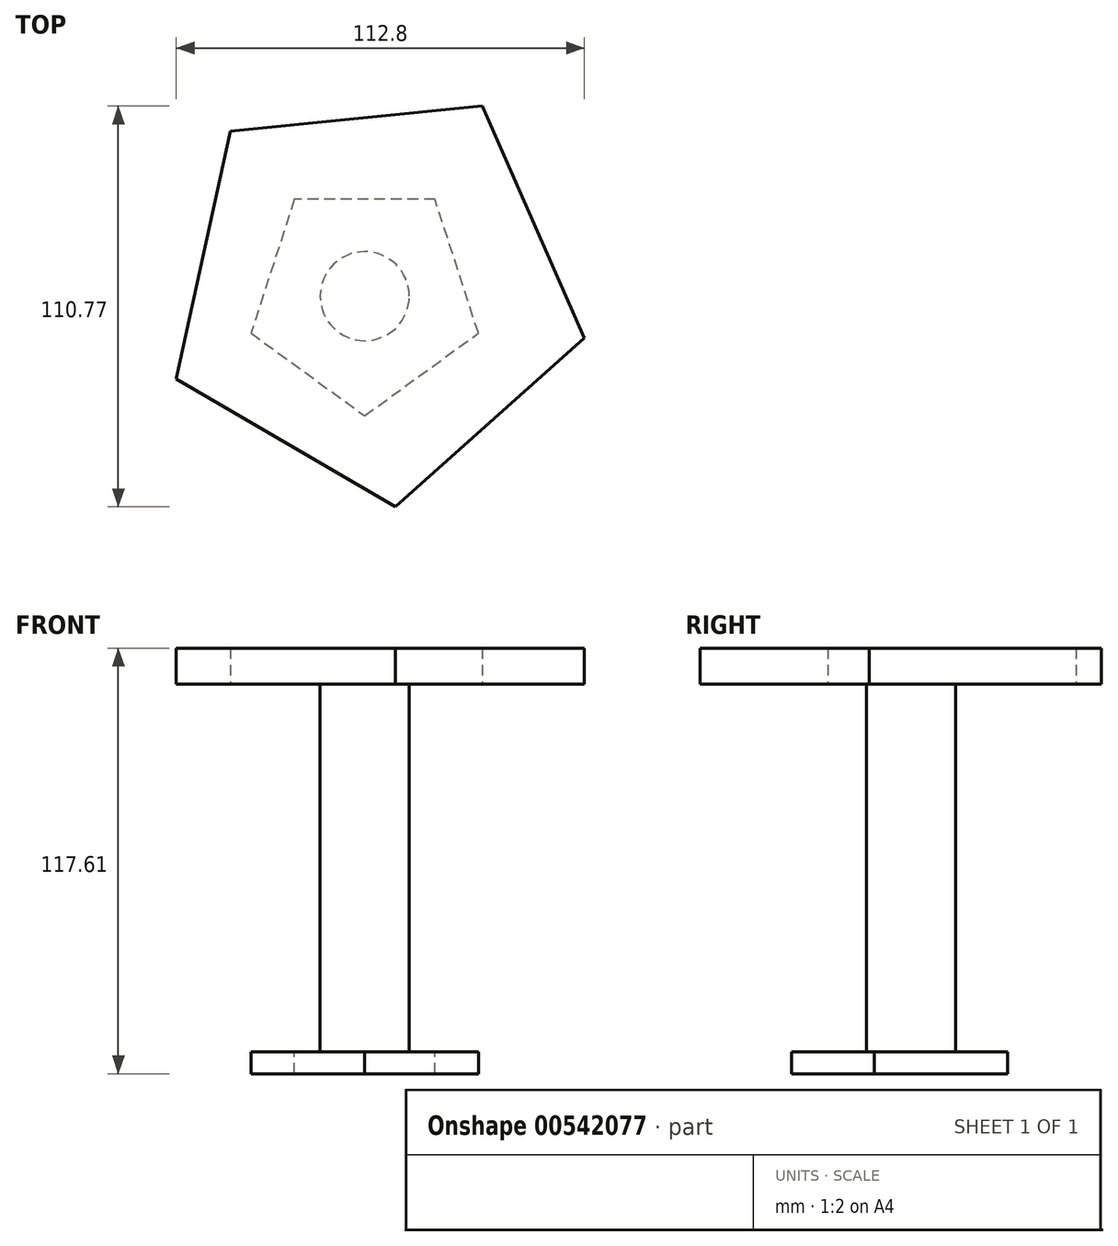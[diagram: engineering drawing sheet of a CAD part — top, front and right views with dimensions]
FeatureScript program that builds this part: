
annotation { "Feature Type Name" : "Feature", "Feature Type Description" : "" }
export const myFeature = defineFeature(function(context is Context, id is Id, definition is map)
    precondition{}
    {
        {
            var Q0;
            Q0=qCreatedBy(makeId("Top.planeOp"),FACE);
            var sketch = newSketch(context, id + "F0", { "sketchPlane" : qUnion([Q0])});
            skCircle(sketch, "E0.cCircle", {"center": v(-117.39, -36.99) * mm, "radius": 48.22 * mm, "construction": true});
            skLineSegment(sketch, "E0.0", {"start": v(-157.06, 7.49) * mm, "end": v(-87.35, 14.48) * mm});
            skLineSegment(sketch, "E0.1", {"start": v(-87.35, 14.48) * mm, "end": v(-59.15, -49.65) * mm});
            skLineSegment(sketch, "E0.2", {"start": v(-59.15, -49.65) * mm, "end": v(-111.43, -96.29) * mm});
            skLineSegment(sketch, "E0.3", {"start": v(-111.43, -96.29) * mm, "end": v(-171.95, -60.98) * mm});
            skLineSegment(sketch, "E0.4", {"start": v(-171.95, -60.98) * mm, "end": v(-157.06, 7.49) * mm});
            skPoint(sketch, "E0.0.midPoint", {"position": v(-122.2, 10.99) * mm});
            skSolve(sketch);
        }
        {
            var Q0;
            Q0 = qSketchRegion(id + "F0", true);
            extrude(context, id + "F1", {"entities" : qUnion([Q0]), "depth" : 9.9 * mm, "offsetDistance" : 25.4 * mm});
        }
        {
            var Q0;
            Q0=makeQuery(id+"F1.opExtrude","CAP_FACE",FACE,{"disambiguationData":[OSD([sQuery(id+"F0.wireOp",EDGE,"E0.0"),sQuery(id+"F0.wireOp",EDGE,"E0.1"),sQuery(id+"F0.wireOp",EDGE,"E0.2"),sQuery(id+"F0.wireOp",EDGE,"E0.3"),sQuery(id+"F0.wireOp",EDGE,"E0.4")])],"isStart":true});
            var sketch = newSketch(context, id + "F2", { "sketchPlane" : qUnion([Q0])});
            skCircle(sketch, "E1", {"center": v(-119.88, 38.06) * mm, "radius": 12.3 * mm});
            skSolve(sketch);
        }
        {
            var Q0;
            Q0 = qSketchRegion(id + "F2", true);
            extrude(context, id + "F3", {"entities" : qUnion([Q0]), "operationType" : NewBodyOperationType.ADD, "depth" : 101.6 * mm, "offsetDistance" : 25.4 * mm});
        }
        {
            var Q0;
            Q0=makeQuery(id+"F3.opExtrude","CAP_FACE",FACE,{"disambiguationData":[OSD([sQuery(id+"F2.wireOp",EDGE,"E1")])],"isStart":false});
            var sketch = newSketch(context, id + "F4", { "sketchPlane" : qUnion([Q0])});
            skCircle(sketch, "E2.cCircle", {"center": v(-119.88, 38.06) * mm, "radius": 26.73 * mm, "construction": true});
            skLineSegment(sketch, "E2.0", {"start": v(-100.46, 11.33) * mm, "end": v(-139.3, 11.33) * mm});
            skLineSegment(sketch, "E2.1", {"start": v(-139.3, 11.33) * mm, "end": v(-151.3, 48.27) * mm});
            skLineSegment(sketch, "E2.2", {"start": v(-151.3, 48.27) * mm, "end": v(-119.88, 71.1) * mm});
            skLineSegment(sketch, "E2.3", {"start": v(-119.88, 71.1) * mm, "end": v(-88.46, 48.27) * mm});
            skLineSegment(sketch, "E2.4", {"start": v(-88.46, 48.27) * mm, "end": v(-100.46, 11.33) * mm});
            skPoint(sketch, "E2.0.midPoint", {"position": v(-119.88, 11.33) * mm});
            skSolve(sketch);
        }
        {
            var Q0;
            Q0 = qSketchRegion(id + "F4", true);
            extrude(context, id + "F5", {"entities" : qUnion([Q0]), "operationType" : NewBodyOperationType.ADD, "depth" : 6.1 * mm, "offsetDistance" : 25.4 * mm});
        }
    });
